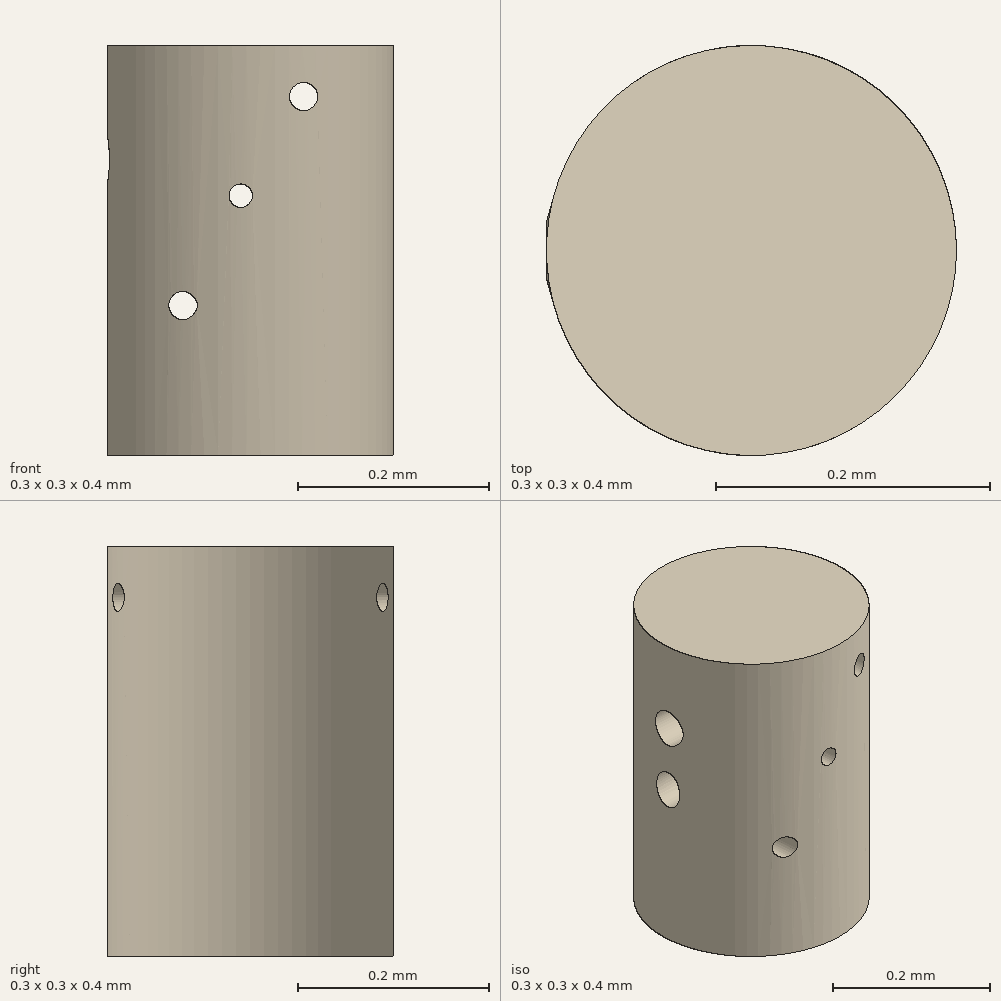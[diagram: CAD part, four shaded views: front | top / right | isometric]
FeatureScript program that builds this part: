
annotation { "Feature Type Name" : "Feature", "Feature Type Description" : "" }
export const myFeature = defineFeature(function(context is Context, id is Id, definition is map)
    precondition{}
    {
        {
            var Q0;
            Q0=qCreatedBy(makeId("Top.planeOp"),FACE);
            var sketch = newSketch(context, id + "F0", { "sketchPlane" : qUnion([Q0])});
            skCircle(sketch, "E0", {"center": v(0, 0) * mm, "radius": 0.15 * mm});
            skSolve(sketch);
        }
        {
            var Q0;
            Q0=qSketchRegion(id+"F0",true);
            extrude(context, id + "F1", {"entities" : qUnion([Q0]), "depth" : 0.43 * mm, "offsetDistance" : 25 * mm});
        }
        {
            var Q0;
            Q0=qCreatedBy(makeId("Top.planeOp"),FACE);
            var sketch = newSketch(context, id + "F2", { "sketchPlane" : qUnion([Q0])});
            skCircle(sketch, "E1", {"center": v(0, 0) * mm, "radius": 0.07 * mm});
            skSolve(sketch);
        }
        {
            var Q0;
            Q0=qSketchRegion(id+"F2",true);
            extrude(context, id + "F3", {"entities" : qUnion([Q0]), "operationType" : NewBodyOperationType.REMOVE, "depth" : 0.1 * mm, "offsetDistance" : 25 * mm});
        }
        {
            var Q0;
            Q0=qCreatedBy(makeId("Front.planeOp"),FACE);
            var sketch = newSketch(context, id + "F4", { "sketchPlane" : qUnion([Q0])});
            skLineSegment(sketch, "E2", {"start": v(0.05, 0.4) * mm, "end": v(-0.1, 0.15) * mm});
            skLineSegment(sketch, "E3", {"start": v(-0.1, 0.15) * mm, "end": v(-0.07, 0.13) * mm});
            skLineSegment(sketch, "E4", {"start": v(0.08, 0.38) * mm, "end": v(0.05, 0.4) * mm});
            skLineSegment(sketch, "E5", {"start": v(-0.02, 0.28) * mm, "end": v(0.84, -0.22) * mm});
            skArc(sketch, "E6", {"start": v(-0.07, 0.13) * mm, "mid": v(0, 0.26) * mm, "end": v(0.08, 0.38) * mm});
            skSolve(sketch);
        }
        {
            var Q0;
            Q0=qSketchRegion(id+"F4",true);
            extrude(context, id + "F5", {"entities" : qUnion([Q0]), "operationType" : NewBodyOperationType.REMOVE, "oppositeDirection" : true, "depth" : 0.05 * mm, "offsetDistance" : 25 * mm});
        }
        {
            var Q0;
            Q0=qSketchRegion(id+"F4",true);
            extrude(context, id + "F6", {"entities" : qUnion([Q0]), "operationType" : NewBodyOperationType.REMOVE, "depth" : 0.05 * mm, "offsetDistance" : 25 * mm});
        }
        {
            var Q0;
            Q0=qCreatedBy(makeId("Front.planeOp"),FACE);
            var sketch = newSketch(context, id + "F7", { "sketchPlane" : qUnion([Q0])});
            skCircle(sketch, "E7", {"center": v(-0.07, 0.16) * mm, "radius": 0.02 * mm});
            skCircle(sketch, "E8", {"center": v(0.06, 0.38) * mm, "radius": 0.02 * mm});
            skCircle(sketch, "E9", {"center": v(-0.01, 0.27) * mm, "radius": 0.01 * mm});
            skSolve(sketch);
        }
        {
            var Q0;
            Q0=qSketchRegion(id+"F7",true);
            extrude(context, id + "F8", {"entities" : qUnion([Q0]), "operationType" : NewBodyOperationType.REMOVE, "oppositeDirection" : true, "depth" : 1 * mm, "offsetDistance" : 25 * mm});
        }
        {
            var Q0;
            Q0=qSketchRegion(id+"F7",true);
            extrude(context, id + "F9", {"entities" : qUnion([Q0]), "operationType" : NewBodyOperationType.REMOVE, "depth" : 1 * mm, "offsetDistance" : 25 * mm});
        }
        {
            var Q0;
            Q0=qCreatedBy(makeId("Right.planeOp"),FACE);
            var sketch = newSketch(context, id + "F10", { "sketchPlane" : qUnion([Q0])});
            skCircle(sketch, "E10", {"center": v(0, 0.31) * mm, "radius": 0.03 * mm});
            skSolve(sketch);
        }
        {
            var Q0;
            Q0=qSketchRegion(id+"F10",true);
            extrude(context, id + "F11", {"entities" : qUnion([Q0]), "operationType" : NewBodyOperationType.REMOVE, "oppositeDirection" : true, "depth" : 1 * mm, "offsetDistance" : 25 * mm});
        }
        {
            var Q0;
            Q0=qSketchRegion(id+"F10",true);
            extrude(context, id + "F12", {"entities" : qUnion([Q0]), "operationType" : NewBodyOperationType.REMOVE, "depth" : 0.01 * mm, "offsetDistance" : 25 * mm});
        }
        {
            var Q0;
            Q0=qCreatedBy(makeId("Right.planeOp"),FACE);
            cPlane(context, id + "F13", {"entities" : qUnion([Q0]), "cplaneType" : CPlaneType.OFFSET, "offset" : 0.15 * mm, "oppositeDirection" : true, "width" : 150 * mm, "height" : 150 * mm});
        }
        {
            var Q0;
            Q0=qCreatedBy(id+"F13.planeOp",FACE);
            var sketch = newSketch(context, id + "F14", { "sketchPlane" : qUnion([Q0])});
            skCircle(sketch, "E11", {"center": v(0, 0.22) * mm, "radius": 0.03 * mm});
            skSolve(sketch);
        }
        {
            var Q0;
            Q0=qSketchRegion(id+"F14",true);
            extrude(context, id + "F15", {"entities" : qUnion([Q0]), "operationType" : NewBodyOperationType.REMOVE, "depth" : 0.1 * mm, "offsetDistance" : 25 * mm});
        }
    });
